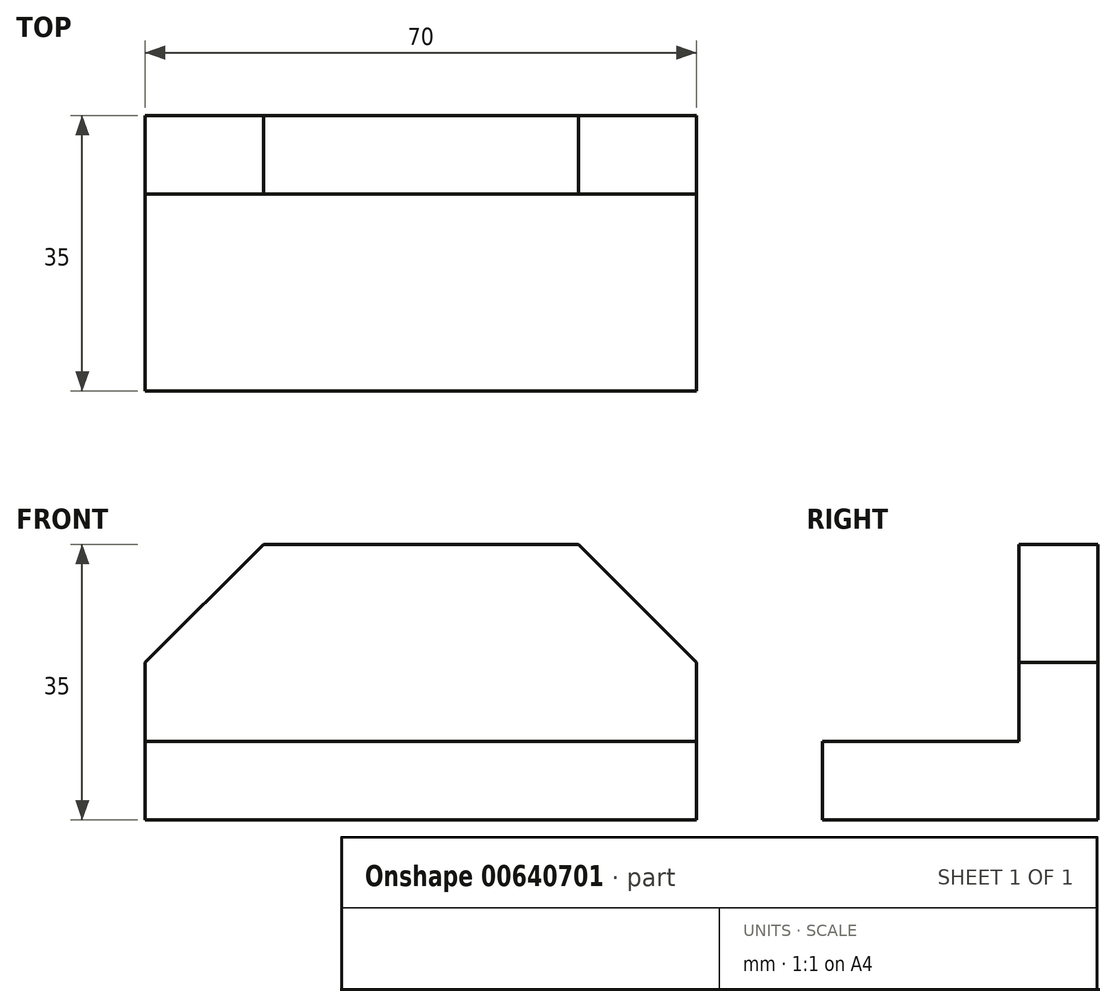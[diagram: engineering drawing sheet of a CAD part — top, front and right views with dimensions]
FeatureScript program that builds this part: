
annotation { "Feature Type Name" : "Feature", "Feature Type Description" : "" }
export const myFeature = defineFeature(function(context is Context, id is Id, definition is map)
    precondition{}
    {
        {
            var Q0;
            Q0=qCreatedBy(makeId("Front.planeOp"),FACE);
            var sketch = newSketch(context, id + "F0", { "sketchPlane" : qUnion([Q0])});
            skLineSegment(sketch, "E0.bottom", {"start": v(-36.83, -35) * mm, "end": v(33.17, -35) * mm});
            skLineSegment(sketch, "E0.top", {"start": v(-36.83, -25) * mm, "end": v(33.17, -25) * mm});
            skLineSegment(sketch, "E0.left", {"start": v(-36.83, -35) * mm, "end": v(-36.83, -25) * mm});
            skLineSegment(sketch, "E0.right", {"start": v(33.17, -35) * mm, "end": v(33.17, -25) * mm});
            skLineSegment(sketch, "E1", {"start": v(-36.83, -25) * mm, "end": v(-36.83, -15) * mm});
            skLineSegment(sketch, "E2", {"start": v(-36.83, -15) * mm, "end": v(-21.83, 0) * mm});
            skLineSegment(sketch, "E3", {"start": v(-21.83, 0) * mm, "end": v(18.17, 0) * mm});
            skLineSegment(sketch, "E4", {"start": v(18.17, 0) * mm, "end": v(33.17, -15) * mm});
            skLineSegment(sketch, "E5", {"start": v(33.17, -15) * mm, "end": v(33.17, -25) * mm});
            skLineSegment(sketch, "E6", {"start": v(-6.83, 0) * mm, "end": v(-6.83, -25) * mm});
            skLineSegment(sketch, "E7", {"start": v(3.17, 0) * mm, "end": v(3.17, -25) * mm});
            skLineSegment(sketch, "E8", {"start": v(-1.83, -25) * mm, "end": v(-1.83, 0) * mm, "construction": true});
            skSolve(sketch);
        }
        {
            var Q0;
            Q0=makeQuery(id+"F0.imprint","IMPRINT",FACE,{"disambiguationData":[TD([[makeQuery(id+"F0.imprint","IMPRINT",EDGE,{"derivedFrom":sQuery(id+"F0.wireOp",EDGE,"E0.bottom")}),1.0]])]});
            extrude(context, id + "F1", {"entities" : qUnion([Q0]), "depth" : 35 * mm, "offsetDistance" : 25 * mm});
        }
        {
            var Q0;
            {var subQ3=sQuery(id+"F0.wireOp",EDGE,"E1");Q0=makeQuery(id+"F0.imprint","IMPRINT",FACE,{"disambiguationData":[TD([[makeQuery(id+"F0.imprint","IMPRINT",EDGE,{"derivedFrom":subQ3}),-1.0]])]});}
            var Q1;
            {var subQ1=sQuery(id+"F0.wireOp",EDGE,"E4");Q1=makeQuery(id+"F0.imprint","IMPRINT",FACE,{"disambiguationData":[TD([[makeQuery(id+"F0.imprint","IMPRINT",EDGE,{"derivedFrom":subQ1}),-1.0]])]});}
            var Q2;
            {var subQ0=sQuery(id+"F0.wireOp",EDGE,"E6");Q2=makeQuery(id+"F0.imprint","IMPRINT",FACE,{"disambiguationData":[TD([[makeQuery(id+"F0.imprint","IMPRINT",EDGE,{"derivedFrom":subQ0}),1.0]])]});}
            extrude(context, id + "F2", {"entities" : qUnion([Q0, Q1, Q2]), "operationType" : NewBodyOperationType.ADD, "depth" : 10 * mm, "offsetDistance" : 25 * mm});
        }
    });
